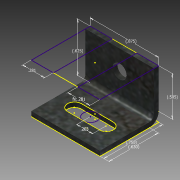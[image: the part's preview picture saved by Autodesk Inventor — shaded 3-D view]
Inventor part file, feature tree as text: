
AUTODESK INVENTOR PART (.ipt)
format: ipt  version: 2015 (Build 190159000, 159)  size: 186,368 bytes
history: native  units: in
note: dims shown in document units (in); Inventor stores cm internally (conversion verified against a paired STEP export)
features: sketch x8, sheet_metal_op x4, projected_geometry x4, other x3, hole x1
ambient origin geometry x8: Origin, YZ Plane, XZ Plane, XY Plane, X Axis, Y Axis, Z Axis, Center Point
bodies: Solid1 (feature_tree)
feature tree (20):
  sheet_metal_op  "Face1"
  sheet_metal_op  "Flange1"
  sketch  "Sketch3"  dims[d3=0.06in]
  hole  "Hole1"  [1 undecoded]
  sketch  "Sketch7"  dims[d5=0.12in]
  sketch  "Sketch8"  dims[d6=0.06in]
  sketch  "Sketch9"  dims[d7=0.625in d8=90.0deg d9=0.06in]
  sketch  "Sketch10"  dims[d10=0.24in d11=0.06in d12=0.06in d13=0.63in d14=0.875in d15=0.875in d16=0.505in d17=0.177in d18=0.75in d19=0.332in d20=0.25in d21=0.5635in d22=0.06in d23=0.8108in d24=0.177in d25=0.146in d26=0.06in d27=0.0in d28=0.625in d29=0.505in d30=0.875in d31=0.75in d32=0.63in d34=0.203in d35=0.281in d36=0.281in]
  sketch  "Sketch1"  dims[d0=0.875in d1=0.75in]
  other  "Plate1"
  sketch  "Sketch2"  dims[d2=0.06in]
  other  "Plate2"
  sheet_metal_op  "Bend1"
  sheet_metal_op  "Corner1"
  projected_geometry  "Projected Loop1"
  sketch  "Sketch4"  dims[d4=0.03in]
  projected_geometry  "Projected Loop2"
  projected_geometry  "Projected Loop3"
  projected_geometry  "Projected Loop4"
  other  "Cut1"
note: 1 required parameter value undecoded (feature->parameter linkage not recoverable at this tier; creation-order binding heuristic only, values carry confidence <= 0.55)
